# Revit family: NaughtOne_VivChair_noarms
name_source: partatom
category: Furniture
units: mm (PartAtom-declared; Revit-internal decimal feet)

## family parameters
Always vertical = Yes
Cut with Voids When Loaded = No
Enable Cutting in Views = No
OmniClass Number = 23.40.20.00
OmniClass Title = General Furniture and Specialties
Render Appearance Source = Family Geometry
Room Calculation Point = No
Shared = Yes
Work Plane-Based = No

## types (2) — shared parameters
Assembly Code = E2020
AssetType = Movable
BIMObjectName = Seating-Casual-Naughtone-Polly_ST4
BarCode = 0.000000
Category = 40.50.12 : Chairs, Seats and Benches
CodePerformance = FISP Certified; ISO14001 Certified
Color = White
ComponentDescription = The Polly chair fundamentally provides a very comfortable ergonomic seat with as little visual detail as possible. The Polypropylene seat shell has subtle edge details, a soft texture and just the right amount of flex, all of which combine to provide a tactile and satisfying sitting experience.
Constituents = Polypropylene; Steel frame
DurationUnit = Years
ExpectedLife = 15-20
Finish = Polyster powder coat; various seat colour finishes available
Keynote = 40.50.12
Manufacturer = naughtone
Material = Glass re-enforced polypropylene; steel frame
ModelNumber = POLLY-CH-ST4
ModelReference = Polly 4 Leg Chair
Mtrl_Seat = <By Category>
NBSReference = 40.50.12
NominalHeight = 30.906 "
NominalLength = 20.866 "
NominalWidth = 20.197 "
Package Qty = 1
Product Documentation Link = http://www.naughtone.com
ReplacementCost = 0.00
SeatHeight = 17.717 "
Shape = Organic
Size = 513mmx530mmx785mm
SustainabilityPerformance = 99% recyclable. 127% recycled & recyclable content
URL = http://www.hermanmiller.com
Uniclass2015 = 40.50.12
Version = 1
WarrantyDescription = 5 year warranty
WarrantyDurationLabor = 5
WarrantyDurationParts = 5
WarrantyDurationUnit = Years
_current revision = 1
_distributed by = www.bimbox.co.uk
zero-valued in all types: Cost, Default Elevation, _BIMspec_GUID

## per-type parameters (varying)
| type | Description | Model | Seat brkt |
| Ganging brackets | Viv Chair sled base chair  no arms no selection ganging brackets | NOVVN100GB | Yes |
| No ganging bracket | Viv Chair sled base chair  no arms no selection no ganging bracket | NOVVN100NG | No |

## geometry (parser evidence)
native form markers: Sweep x5
no freeform markers — native parametric forms only
